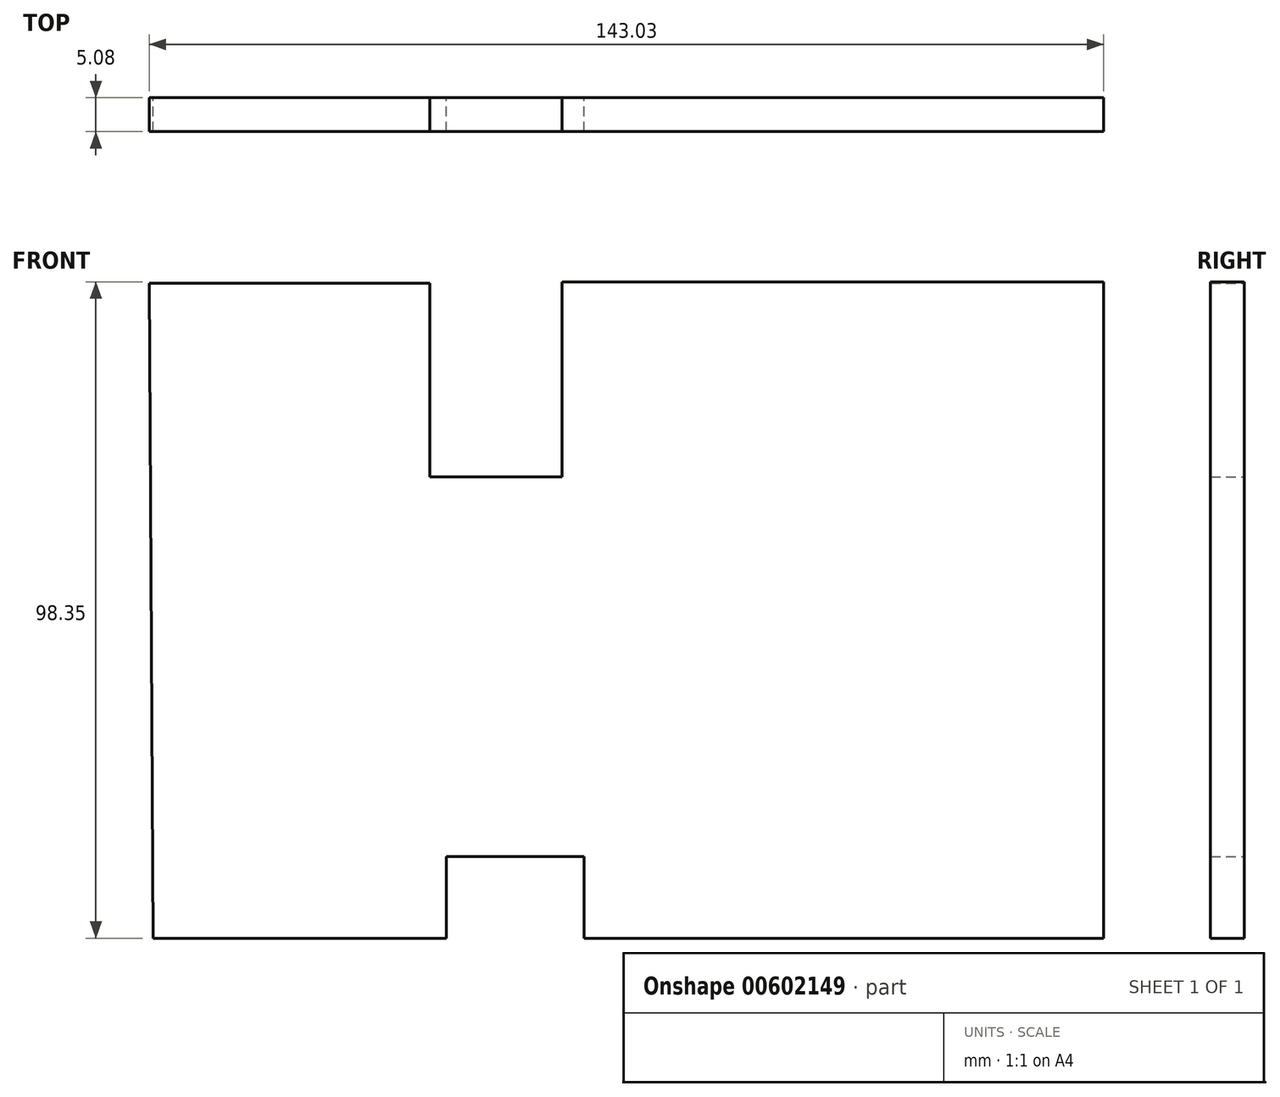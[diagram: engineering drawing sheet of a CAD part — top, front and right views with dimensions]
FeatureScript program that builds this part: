
annotation { "Feature Type Name" : "Feature", "Feature Type Description" : "" }
export const myFeature = defineFeature(function(context is Context, id is Id, definition is map)
    precondition{}
    {
        {
            var Q0;
            Q0=qCreatedBy(makeId("Front.planeOp"),FACE);
            var sketch = newSketch(context, id + "F0", { "sketchPlane" : qUnion([Q0])});
            skLineSegment(sketch, "E0", {"start": v(-76.29, 55.85) * mm, "end": v(-34.28, 55.85) * mm});
            skLineSegment(sketch, "E1", {"start": v(-34.28, 55.85) * mm, "end": v(-34.28, 26.83) * mm});
            skLineSegment(sketch, "E2", {"start": v(-34.28, 26.83) * mm, "end": v(-14.42, 26.83) * mm});
            skLineSegment(sketch, "E3", {"start": v(-14.42, 26.83) * mm, "end": v(-14.42, 56.05) * mm});
            skLineSegment(sketch, "E4", {"start": v(-14.42, 56.05) * mm, "end": v(66.74, 56.05) * mm});
            skLineSegment(sketch, "E5", {"start": v(66.74, 56.05) * mm, "end": v(66.74, -42.3) * mm});
            skLineSegment(sketch, "E6", {"start": v(66.74, -42.3) * mm, "end": v(-11.17, -42.3) * mm});
            skLineSegment(sketch, "E7", {"start": v(-11.17, -42.3) * mm, "end": v(-11.17, -30.08) * mm});
            skLineSegment(sketch, "E8", {"start": v(-11.17, -30.08) * mm, "end": v(-31.8, -30.08) * mm});
            skLineSegment(sketch, "E9", {"start": v(-31.8, -30.08) * mm, "end": v(-31.8, -42.3) * mm});
            skLineSegment(sketch, "E10", {"start": v(-31.8, -42.3) * mm, "end": v(-75.71, -42.3) * mm});
            skLineSegment(sketch, "E11", {"start": v(-75.71, -42.3) * mm, "end": v(-76.29, 55.85) * mm});
            skSolve(sketch);
        }
        {
            var Q0;
            Q0=makeQuery(id+"F0.imprint","IMPRINT",FACE,{"disambiguationData":[TD([[makeQuery(id+"F0.imprint","IMPRINT",EDGE,{"derivedFrom":sQuery(id+"F0.wireOp",EDGE,"E0")}),-1.0]])]});
            extrude(context, id + "F1", {"entities" : qUnion([Q0]), "depth" : 5.08 * mm, "offsetDistance" : 25.4 * mm});
        }
    });
